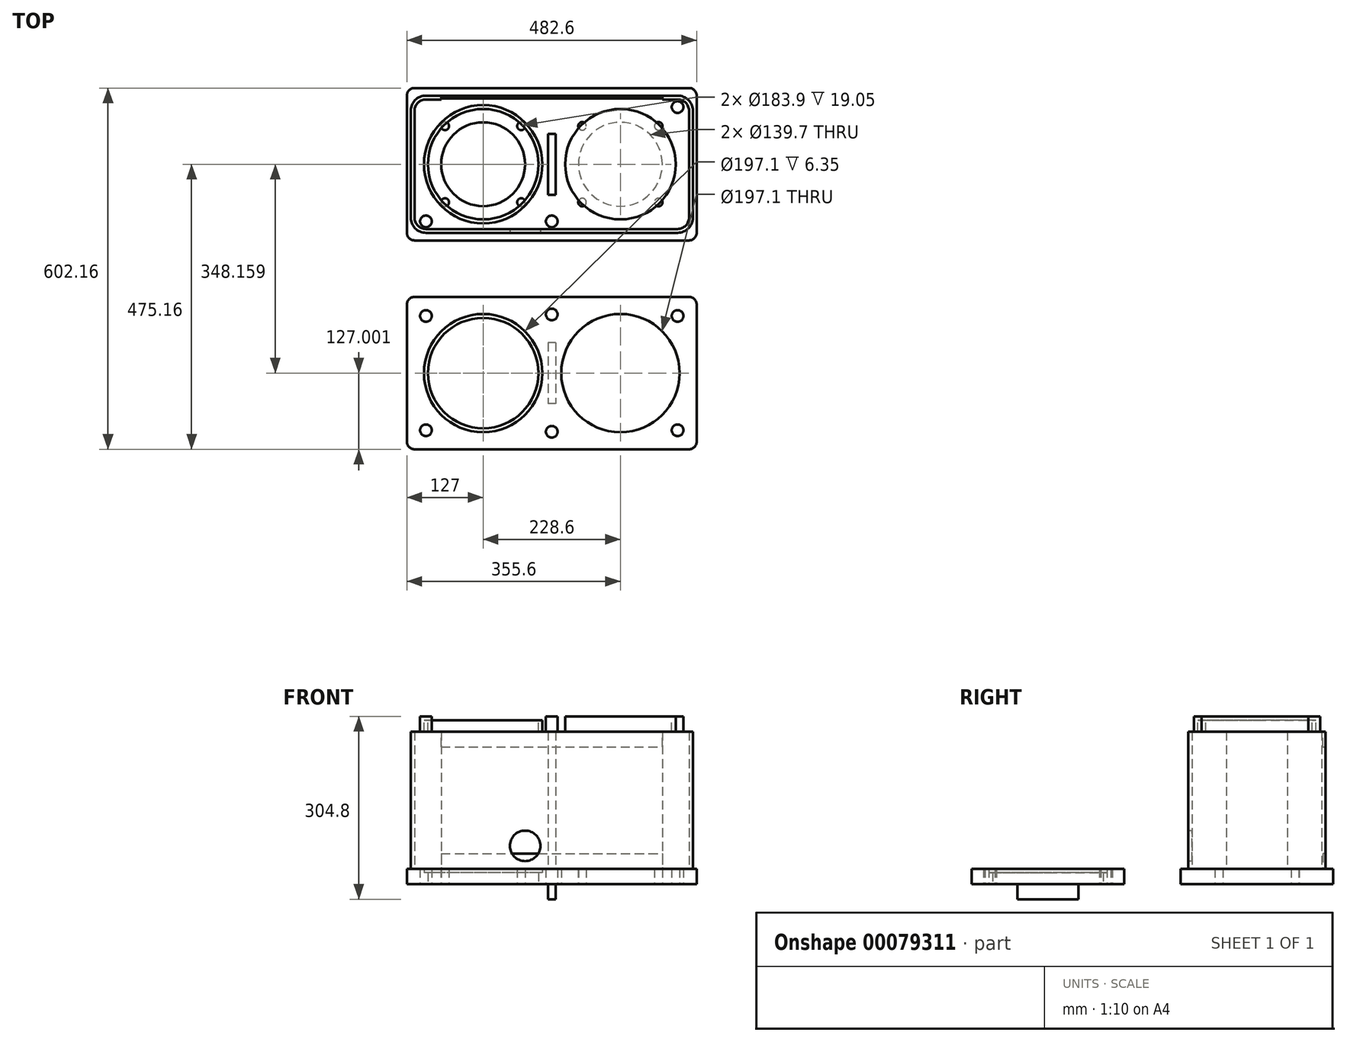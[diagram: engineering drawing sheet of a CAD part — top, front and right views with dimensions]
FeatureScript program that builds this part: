
annotation { "Feature Type Name" : "Feature", "Feature Type Description" : "" }
export const myFeature = defineFeature(function(context is Context, id is Id, definition is map)
    precondition{}
    {
        {
            var Q0;
            Q0=qCreatedBy(makeId("Top.planeOp"),FACE);
            var sketch = newSketch(context, id + "F0", { "sketchPlane" : qUnion([Q0])});
            skLineSegment(sketch, "E0.bottom", {"start": v(241.3, -127) * mm, "end": v(-241.3, -127) * mm});
            skLineSegment(sketch, "E0.top", {"start": v(241.3, 127) * mm, "end": v(-241.3, 127) * mm});
            skLineSegment(sketch, "E0.left", {"start": v(241.3, -127) * mm, "end": v(241.3, 127) * mm});
            skLineSegment(sketch, "E0.right", {"start": v(-241.3, -127) * mm, "end": v(-241.3, 127) * mm});
            skPoint(sketch, "E0.middle", {"position": v(0, 0) * mm});
            skSolve(sketch);
        }
        {
            var Q0;
            Q0=makeQuery(id+"F0.imprint","IMPRINT",FACE,{"disambiguationData":[TD([[makeQuery(id+"F0.imprint","IMPRINT",EDGE,{"derivedFrom":sQuery(id+"F0.wireOp",EDGE,"E0.bottom")}),-1.0]])]});
            extrude(context, id + "F1", {"entities" : qUnion([Q0]), "depth" : 25.4 * mm});
        }
        {
            var Q0;
            Q0=makeQuery(id+"F1.opExtrude","CAP_FACE",FACE,{"disambiguationData":[OSD([sQuery(id+"F0.wireOp",EDGE,"E0.bottom"),sQuery(id+"F0.wireOp",EDGE,"E0.top"),sQuery(id+"F0.wireOp",EDGE,"E0.left"),sQuery(id+"F0.wireOp",EDGE,"E0.right")])],"isStart":false});
            var sketch = newSketch(context, id + "F2", { "sketchPlane" : qUnion([Q0])});
            skLineSegment(sketch, "E1.bottom", {"start": v(209.55, -114.3) * mm, "end": v(-209.55, -114.3) * mm});
            skLineSegment(sketch, "E1.left", {"start": v(234.95, -88.9) * mm, "end": v(234.95, 88.9) * mm});
            skLineSegment(sketch, "E1.right", {"start": v(-234.95, -88.9) * mm, "end": v(-234.95, 88.9) * mm});
            skPoint(sketch, "E1.middle", {"position": v(0, 0) * mm});
            skLineSegment(sketch, "E2.bottom", {"start": v(209.55, -107.95) * mm, "end": v(-209.55, -107.95) * mm});
            skLineSegment(sketch, "E2.left", {"start": v(228.6, -88.9) * mm, "end": v(228.6, 88.9) * mm});
            skLineSegment(sketch, "E2.right", {"start": v(-228.6, -88.9) * mm, "end": v(-228.6, 88.9) * mm});
            skLineSegment(sketch, "E3", {"start": v(-209.55, 114.3) * mm, "end": v(-184.15, 114.3) * mm});
            skLineSegment(sketch, "E4", {"start": v(-209.55, 107.95) * mm, "end": v(-184.14, 107.95) * mm});
            skLineSegment(sketch, "E5", {"start": v(-184.15, 114.3) * mm, "end": v(-184.14, 107.95) * mm});
            skLineSegment(sketch, "E6", {"start": v(209.55, 114.3) * mm, "end": v(184.15, 114.3) * mm});
            skLineSegment(sketch, "E7", {"start": v(184.15, 114.3) * mm, "end": v(184.15, 107.95) * mm});
            skLineSegment(sketch, "E8", {"start": v(184.15, 107.95) * mm, "end": v(209.55, 107.95) * mm});
            skPoint(sketch, "E9.visualSharp", {"position": v(-234.95, 114.3) * mm});
            skArc(sketch, "E9.filletArc", {"start": v(-209.55, 114.3) * mm, "mid": v(-227.51, 106.86) * mm, "end": v(-234.95, 88.9) * mm});
            skPoint(sketch, "E10.visualSharp", {"position": v(-234.95, -114.3) * mm});
            skArc(sketch, "E10.filletArc", {"start": v(-234.95, -88.9) * mm, "mid": v(-227.51, -106.86) * mm, "end": v(-209.55, -114.3) * mm});
            skPoint(sketch, "E11.visualSharp", {"position": v(234.95, -114.3) * mm});
            skArc(sketch, "E11.filletArc", {"start": v(209.55, -114.3) * mm, "mid": v(227.51, -106.86) * mm, "end": v(234.95, -88.9) * mm});
            skPoint(sketch, "E12.visualSharp", {"position": v(234.95, 114.3) * mm});
            skArc(sketch, "E12.filletArc", {"start": v(234.95, 88.9) * mm, "mid": v(227.51, 106.86) * mm, "end": v(209.55, 114.3) * mm});
            skPoint(sketch, "E13.visualSharp", {"position": v(-228.6, 107.95) * mm});
            skArc(sketch, "E13.filletArc", {"start": v(-209.55, 107.95) * mm, "mid": v(-223.02, 102.37) * mm, "end": v(-228.6, 88.9) * mm});
            skPoint(sketch, "E14.visualSharp", {"position": v(-228.6, -107.95) * mm});
            skArc(sketch, "E14.filletArc", {"start": v(-228.6, -88.9) * mm, "mid": v(-223.02, -102.37) * mm, "end": v(-209.55, -107.95) * mm});
            skPoint(sketch, "E15.visualSharp", {"position": v(228.6, -107.95) * mm});
            skArc(sketch, "E15.filletArc", {"start": v(209.55, -107.95) * mm, "mid": v(223.02, -102.37) * mm, "end": v(228.6, -88.9) * mm});
            skPoint(sketch, "E16.visualSharp", {"position": v(228.6, 107.95) * mm});
            skArc(sketch, "E16.filletArc", {"start": v(228.6, 88.9) * mm, "mid": v(223.02, 102.37) * mm, "end": v(209.55, 107.95) * mm});
            skLineSegment(sketch, "E17.bottom", {"start": v(6.35, -50.8) * mm, "end": v(-6.35, -50.8) * mm});
            skLineSegment(sketch, "E17.top", {"start": v(6.35, 50.8) * mm, "end": v(-6.35, 50.8) * mm});
            skLineSegment(sketch, "E17.left", {"start": v(6.35, -50.8) * mm, "end": v(6.35, 50.8) * mm});
            skLineSegment(sketch, "E17.right", {"start": v(-6.35, -50.8) * mm, "end": v(-6.35, 50.8) * mm});
            skSolve(sketch);
        }
        {
            var Q0;
            Q0=makeQuery(id+"F2.imprint","IMPRINT",FACE,{"disambiguationData":[TD([[makeQuery(id+"F2.imprint","IMPRINT",EDGE,{"derivedFrom":sQuery(id+"F2.wireOp",EDGE,"E1.bottom")}),-1.0]])]});
            var Q1;
            Q1=makeQuery(id+"F2.imprint","IMPRINT",FACE,{"disambiguationData":[TD([[makeQuery(id+"F2.imprint","IMPRINT",EDGE,{"derivedFrom":sQuery(id+"F2.wireOp",EDGE,"E17.bottom")}),-1.0]])]});
            extrude(context, id + "F3", {"entities" : qUnion([Q0, Q1]), "operationType" : NewBodyOperationType.ADD, "depth" : 228.6 * mm});
        }
        {
            var Q0;
            Q0=makeQuery(id+"F3.opExtrude","CAP_FACE",FACE,{"disambiguationData":[OSD([sQuery(id+"F2.wireOp",EDGE,"E1.bottom"),sQuery(id+"F2.wireOp",EDGE,"E1.left"),sQuery(id+"F2.wireOp",EDGE,"E1.right"),sQuery(id+"F2.wireOp",EDGE,"E2.bottom"),sQuery(id+"F2.wireOp",EDGE,"E2.left"),sQuery(id+"F2.wireOp",EDGE,"E2.right"),sQuery(id+"F2.wireOp",EDGE,"E3"),sQuery(id+"F2.wireOp",EDGE,"E4"),sQuery(id+"F2.wireOp",EDGE,"E5"),sQuery(id+"F2.wireOp",EDGE,"E6"),sQuery(id+"F2.wireOp",EDGE,"E7"),sQuery(id+"F2.wireOp",EDGE,"E8"),sQuery(id+"F2.wireOp",EDGE,"E9.filletArc"),sQuery(id+"F2.wireOp",EDGE,"E10.filletArc"),sQuery(id+"F2.wireOp",EDGE,"E11.filletArc"),sQuery(id+"F2.wireOp",EDGE,"E12.filletArc"),sQuery(id+"F2.wireOp",EDGE,"E13.filletArc"),sQuery(id+"F2.wireOp",EDGE,"E14.filletArc"),sQuery(id+"F2.wireOp",EDGE,"E15.filletArc"),sQuery(id+"F2.wireOp",EDGE,"E16.filletArc")])],"isStart":false});
            var sketch = newSketch(context, id + "F4", { "sketchPlane" : qUnion([Q0])});
            skLineSegment(sketch, "E18.bottom", {"start": v(241.3, -127) * mm, "end": v(-241.3, -127) * mm});
            skLineSegment(sketch, "E18.top", {"start": v(241.3, 127) * mm, "end": v(-241.3, 127) * mm});
            skLineSegment(sketch, "E18.left", {"start": v(241.3, -127) * mm, "end": v(241.3, 127) * mm});
            skLineSegment(sketch, "E18.right", {"start": v(-241.3, -127) * mm, "end": v(-241.3, 127) * mm});
            skPoint(sketch, "E18.middle", {"position": v(0, 0) * mm});
            skSolve(sketch);
        }
        {
            var Q0;
            Q0=qSketchRegion(id+"F4",true);
            extrude(context, id + "F5", {"entities" : qUnion([Q0]), "operationType" : NewBodyOperationType.ADD, "depth" : 25.4 * mm});
        }
        {
            var Q0;
            Q0=makeQuery(id+"F3.opExtrude","SWEPT_FACE",FACE,{"disambiguationData":[OSD([sQuery(id+"F2.wireOp",EDGE,"E1.bottom")])]});
            var sketch = newSketch(context, id + "F6", { "sketchPlane" : qUnion([Q0])});
            skCircle(sketch, "E19", {"center": v(-44.45, 63.5) * mm, "radius": 25.4 * mm});
            skSolve(sketch);
        }
        {
            var Q0;
            Q0=makeQuery(id+"F6.imprint","IMPRINT",FACE,{"disambiguationData":[TD([[makeQuery(id+"F6.imprint","IMPRINT",EDGE,{"derivedFrom":sQuery(id+"F6.wireOp",EDGE,"E19")}),1.0]])]});
            extrude(context, id + "F7", {"entities" : qUnion([Q0]), "operationType" : NewBodyOperationType.REMOVE, "oppositeDirection" : true, "depth" : 6.35 * mm});
        }
        {
            var Q0;
            Q0=qCreatedBy(makeId("Right.planeOp"),FACE);
            var sketch = newSketch(context, id + "F8", { "sketchPlane" : qUnion([Q0])});
            skLineSegment(sketch, "E20", {"start": v(0, -47.78) * mm, "end": v(0, 307.42) * mm, "construction": true});
            skSolve(sketch);
        }
        {
            var Q0;
            Q0=makeQuery(id+"F5.opExtrude","CAP_FACE",FACE,{"disambiguationData":[OSD([sQuery(id+"F4.wireOp",EDGE,"E18.bottom"),sQuery(id+"F4.wireOp",EDGE,"E18.top"),sQuery(id+"F4.wireOp",EDGE,"E18.left"),sQuery(id+"F4.wireOp",EDGE,"E18.right")])],"isStart":false});
            var sketch = newSketch(context, id + "F9", { "sketchPlane" : qUnion([Q0])});
            skLineSegment(sketch, "E21", {"start": v(0, 148.36) * mm, "end": v(0, -160.24) * mm, "construction": true});
            skPoint(sketch, "E21.endSnap0", {"position": v(0, -127) * mm});
            skLineSegment(sketch, "E22", {"start": v(-277.11, 0) * mm, "end": v(283.69, 0) * mm, "construction": true});
            skPoint(sketch, "E22.startSnap0", {"position": v(-241.3, 0) * mm});
            skPoint(sketch, "E22.endSnap0", {"position": v(-241.3, 0) * mm});
            skCircle(sketch, "E23", {"center": v(-114.3, 0) * mm, "radius": 98.55 * mm});
            skCircle(sketch, "E24", {"center": v(-114.3, 0) * mm, "radius": 91.95 * mm});
            skCircle(sketch, "E25", {"center": v(-209.55, 95.25) * mm, "radius": 9.72 * mm});
            skCircle(sketch, "E26", {"center": v(0, 95.25) * mm, "radius": 9.72 * mm});
            skCircle(sketch, "E27.MirrorC", {"center": v(114.3, 0) * mm, "radius": 98.55 * mm});
            skCircle(sketch, "E28.MirrorC", {"center": v(114.3, 0) * mm, "radius": 91.95 * mm});
            skCircle(sketch, "E29.MirrorC", {"center": v(209.55, 95.25) * mm, "radius": 9.72 * mm});
            skCircle(sketch, "E30.MirrorC", {"center": v(-209.55, -95.25) * mm, "radius": 9.72 * mm});
            skCircle(sketch, "E31.MirrorC", {"center": v(0, -95.25) * mm, "radius": 9.72 * mm});
            skCircle(sketch, "E32.MirrorC", {"center": v(209.55, -95.25) * mm, "radius": 9.72 * mm});
            skSolve(sketch);
        }
        {
            var Q0;
            Q0=makeQuery(id+"F9.imprint","IMPRINT",FACE,{"disambiguationData":[TD([[makeQuery(id+"F9.imprint","IMPRINT",EDGE,{"derivedFrom":sQuery(id+"F9.wireOp",EDGE,"E25")}),1.0]])]});
            var Q1;
            Q1=makeQuery(id+"F9.imprint","IMPRINT",FACE,{"disambiguationData":[TD([[makeQuery(id+"F9.imprint","IMPRINT",EDGE,{"derivedFrom":sQuery(id+"F9.wireOp",EDGE,"E26")}),1.0]])]});
            var Q2;
            Q2=makeQuery(id+"F9.imprint","IMPRINT",FACE,{"disambiguationData":[TD([[makeQuery(id+"F9.imprint","IMPRINT",EDGE,{"derivedFrom":sQuery(id+"F9.wireOp",EDGE,"E24")}),1.0]])]});
            var Q3;
            Q3=makeQuery(id+"F9.imprint","IMPRINT",FACE,{"disambiguationData":[TD([[makeQuery(id+"F9.imprint","IMPRINT",EDGE,{"derivedFrom":sQuery(id+"F9.wireOp",EDGE,"E28.MirrorC")}),-1.0]])]});
            var Q4;
            Q4=makeQuery(id+"F9.imprint","IMPRINT",FACE,{"disambiguationData":[TD([[makeQuery(id+"F9.imprint","IMPRINT",EDGE,{"derivedFrom":sQuery(id+"F9.wireOp",EDGE,"E29.MirrorC")}),-1.0]])]});
            var Q5;
            Q5=makeQuery(id+"F9.imprint","IMPRINT",FACE,{"disambiguationData":[TD([[makeQuery(id+"F9.imprint","IMPRINT",EDGE,{"derivedFrom":sQuery(id+"F9.wireOp",EDGE,"E32.MirrorC")}),1.0]])]});
            var Q6;
            Q6=makeQuery(id+"F9.imprint","IMPRINT",FACE,{"disambiguationData":[TD([[makeQuery(id+"F9.imprint","IMPRINT",EDGE,{"derivedFrom":sQuery(id+"F9.wireOp",EDGE,"E31.MirrorC")}),-1.0]])]});
            var Q7;
            Q7=makeQuery(id+"F9.imprint","IMPRINT",FACE,{"disambiguationData":[TD([[makeQuery(id+"F9.imprint","IMPRINT",EDGE,{"derivedFrom":sQuery(id+"F9.wireOp",EDGE,"E30.MirrorC")}),-1.0]])]});
            extrude(context, id + "F10", {"entities" : qUnion([Q0, Q1, Q2, Q3, Q4, Q5, Q6, Q7]), "operationType" : NewBodyOperationType.REMOVE, "oppositeDirection" : true, "depth" : 25.4 * mm});
        }
        {
            var Q0;
            Q0=makeQuery(id+"F9.imprint","IMPRINT",FACE,{"disambiguationData":[TD([[makeQuery(id+"F9.imprint","IMPRINT",EDGE,{"derivedFrom":sQuery(id+"F9.wireOp",EDGE,"E23")}),1.0]])]});
            var Q1;
            Q1=makeQuery(id+"F9.imprint","IMPRINT",FACE,{"disambiguationData":[TD([[makeQuery(id+"F9.imprint","IMPRINT",EDGE,{"derivedFrom":sQuery(id+"F9.wireOp",EDGE,"E27.MirrorC")}),-1.0]])]});
            extrude(context, id + "F11", {"entities" : qUnion([Q0, Q1]), "operationType" : NewBodyOperationType.REMOVE, "oppositeDirection" : true, "depth" : 6.35 * mm});
        }
        {
            var Q0;
            Q0=makeQuery(id+"F1.opExtrude","CAP_FACE",FACE,{"disambiguationData":[OSD([sQuery(id+"F0.wireOp",EDGE,"E0.bottom"),sQuery(id+"F0.wireOp",EDGE,"E0.top"),sQuery(id+"F0.wireOp",EDGE,"E0.left"),sQuery(id+"F0.wireOp",EDGE,"E0.right")])],"isStart":true});
            var sketch = newSketch(context, id + "F12", { "sketchPlane" : qUnion([Q0])});
            skLineSegment(sketch, "E33", {"start": v(270.27, 0) * mm, "end": v(-270.6, 0) * mm, "construction": true});
            skPoint(sketch, "E33.endSnap0", {"position": v(241.3, 0) * mm});
            skLineSegment(sketch, "E34", {"start": v(0, -143.09) * mm, "end": v(0, 149.51) * mm, "construction": true});
            skPoint(sketch, "E34.endSnap0", {"position": v(0, 127) * mm});
            skCircle(sketch, "E35", {"center": v(114.3, 0) * mm, "radius": 69.85 * mm});
            skLineSegment(sketch, "E36", {"start": v(114.3, 0) * mm, "end": v(177.8, -63.5) * mm, "construction": true});
            skCircle(sketch, "E37", {"center": v(177.8, -63.5) * mm, "radius": 6.75 * mm});
            skCircle(sketch, "E38.1.0", {"center": v(177.8, 63.5) * mm, "radius": 6.75 * mm});
            skCircle(sketch, "E38.2.0", {"center": v(50.8, 63.5) * mm, "radius": 6.75 * mm});
            skCircle(sketch, "E38.3.0", {"center": v(50.8, -63.5) * mm, "radius": 6.75 * mm});
            skCircle(sketch, "E39.MirrorC", {"center": v(-50.8, -63.5) * mm, "radius": 6.75 * mm});
            skCircle(sketch, "E40.MirrorC", {"center": v(-114.3, 0) * mm, "radius": 69.85 * mm});
            skCircle(sketch, "E41.MirrorC", {"center": v(-50.8, 63.5) * mm, "radius": 6.75 * mm});
            skCircle(sketch, "E42.MirrorC", {"center": v(-177.8, 63.5) * mm, "radius": 6.75 * mm});
            skCircle(sketch, "E43.MirrorC", {"center": v(-177.8, -63.5) * mm, "radius": 6.75 * mm});
            skSolve(sketch);
        }
        {
            var Q0;
            Q0 = qSketchRegion(id + "F12", true);
            extrude(context, id + "F13", {"entities" : qUnion([Q0]), "operationType" : NewBodyOperationType.REMOVE, "oppositeDirection" : true, "depth" : 25.4 * mm});
        }
        {
            var Q0;
            Q0=makeQuery(id+"F1.opExtrude","CAP_FACE",FACE,{"disambiguationData":[OSD([sQuery(id+"F0.wireOp",EDGE,"E0.bottom"),sQuery(id+"F0.wireOp",EDGE,"E0.top"),sQuery(id+"F0.wireOp",EDGE,"E0.left"),sQuery(id+"F0.wireOp",EDGE,"E0.right")])],"isStart":false});
            var sketch = newSketch(context, id + "F14", { "sketchPlane" : qUnion([Q0])});
            skLineSegment(sketch, "E44.bottom", {"start": v(-184.15, 114.3) * mm, "end": v(184.15, 114.3) * mm});
            skLineSegment(sketch, "E44.top", {"start": v(-184.15, 109.54) * mm, "end": v(184.15, 109.54) * mm});
            skLineSegment(sketch, "E44.left", {"start": v(-184.15, 114.3) * mm, "end": v(-184.15, 109.54) * mm});
            skLineSegment(sketch, "E44.right", {"start": v(184.15, 114.3) * mm, "end": v(184.15, 109.54) * mm});
            skSolve(sketch);
        }
        {
            var Q0;
            {var subQ0=sQuery(id+"F14.wireOp",EDGE,"E44.bottom");Q0=makeQuery(id+"F14.imprint","IMPRINT",FACE,{"disambiguationData":[TD([[makeQuery(id+"F14.imprint","IMPRINT",EDGE,{"derivedFrom":subQ0}),-1.0]])]});}
            extrude(context, id + "F15", {"entities" : qUnion([Q0]), "depth" : 25.4 * mm});
        }
        {
            var Q0;
            Q0=makeQuery(id+"F5.opExtrude","CAP_FACE",FACE,{"disambiguationData":[OSD([sQuery(id+"F4.wireOp",EDGE,"E18.bottom"),sQuery(id+"F4.wireOp",EDGE,"E18.top"),sQuery(id+"F4.wireOp",EDGE,"E18.left"),sQuery(id+"F4.wireOp",EDGE,"E18.right")])],"isStart":true});
            var sketch = newSketch(context, id + "F16", { "sketchPlane" : qUnion([Q0])});
            skLineSegment(sketch, "E45.bottom", {"start": v(-184.15, -109.54) * mm, "end": v(184.15, -109.54) * mm});
            skLineSegment(sketch, "E45.top", {"start": v(-184.15, -114.3) * mm, "end": v(184.15, -114.3) * mm});
            skLineSegment(sketch, "E45.left", {"start": v(-184.15, -109.54) * mm, "end": v(-184.15, -114.3) * mm});
            skLineSegment(sketch, "E45.right", {"start": v(184.15, -109.54) * mm, "end": v(184.15, -114.3) * mm});
            skPoint(sketch, "E45.middle", {"position": v(0, -111.92) * mm});
            skSolve(sketch);
        }
        {
            var Q0;
            {var subQ4=sQuery(id+"F16.wireOp",EDGE,"E45.top");Q0=makeQuery(id+"F16.imprint","IMPRINT",FACE,{"disambiguationData":[TD([[makeQuery(id+"F16.imprint","IMPRINT",EDGE,{"derivedFrom":subQ4}),1.0]])]});}
            extrude(context, id + "F17", {"entities" : qUnion([Q0]), "depth" : 25.4 * mm});
        }
        {
            var Q0;
            Q0=qCreatedBy(makeId("Top.planeOp"),FACE);
            var sketch = newSketch(context, id + "F18", { "sketchPlane" : qUnion([Q0])});
            skLineSegment(sketch, "E46.bottom", {"start": v(241.3, -475.16) * mm, "end": v(-241.3, -475.16) * mm});
            skLineSegment(sketch, "E46.top", {"start": v(241.3, -221.16) * mm, "end": v(-241.3, -221.16) * mm});
            skLineSegment(sketch, "E46.left", {"start": v(241.3, -475.16) * mm, "end": v(241.3, -221.16) * mm});
            skLineSegment(sketch, "E46.right", {"start": v(-241.3, -475.16) * mm, "end": v(-241.3, -221.16) * mm});
            skPoint(sketch, "E46.middle", {"position": v(0, -348.16) * mm});
            skLineSegment(sketch, "E47", {"start": v(0, -197.28) * mm, "end": v(0, -505.88) * mm, "construction": true});
            skPoint(sketch, "E47.endSnap0", {"position": v(0, -472.64) * mm});
            skLineSegment(sketch, "E48", {"start": v(-277.11, -348.16) * mm, "end": v(283.69, -348.16) * mm, "construction": true});
            skPoint(sketch, "E48.startSnap0", {"position": v(-247.65, -348.16) * mm});
            skPoint(sketch, "E48.endSnap0", {"position": v(-247.65, -348.16) * mm});
            skCircle(sketch, "E49", {"center": v(-114.3, -348.16) * mm, "radius": 98.55 * mm});
            skCircle(sketch, "E50", {"center": v(-114.3, -348.16) * mm, "radius": 91.95 * mm});
            skCircle(sketch, "E51", {"center": v(-209.55, -252.9) * mm, "radius": 9.72 * mm});
            skCircle(sketch, "E52", {"center": v(0, -250.39) * mm, "radius": 9.72 * mm});
            skCircle(sketch, "E53.MirrorC", {"center": v(114.3, -348.16) * mm, "radius": 98.55 * mm});
            skCircle(sketch, "E54.MirrorC", {"center": v(114.3, -348.16) * mm, "radius": 91.95 * mm});
            skCircle(sketch, "E55.MirrorC", {"center": v(209.55, -252.9) * mm, "radius": 9.72 * mm});
            skCircle(sketch, "E56.MirrorC", {"center": v(-209.55, -443.4) * mm, "radius": 9.72 * mm});
            skCircle(sketch, "E57.MirrorC", {"center": v(0, -445.93) * mm, "radius": 9.72 * mm});
            skCircle(sketch, "E58.MirrorC", {"center": v(209.55, -443.4) * mm, "radius": 9.72 * mm});
            skSolve(sketch);
        }
        {
            var Q0;
            Q0=makeQuery(id+"F18.imprint","IMPRINT",FACE,{"disambiguationData":[TD([[makeQuery(id+"F18.imprint","IMPRINT",EDGE,{"derivedFrom":sQuery(id+"F18.wireOp",EDGE,"E46.bottom")}),-1.0]])]});
            extrude(context, id + "F19", {"entities" : qUnion([Q0]), "depth" : 25.4 * mm});
        }
        {
            var Q0;
            Q0=makeQuery(id+"F18.imprint","IMPRINT",FACE,{"disambiguationData":[TD([[makeQuery(id+"F18.imprint","IMPRINT",EDGE,{"derivedFrom":sQuery(id+"F18.wireOp",EDGE,"E53.MirrorC")}),-1.0]])]});
            var Q1;
            Q1=makeQuery(id+"F18.imprint","IMPRINT",FACE,{"disambiguationData":[TD([[makeQuery(id+"F18.imprint","IMPRINT",EDGE,{"derivedFrom":sQuery(id+"F18.wireOp",EDGE,"E49")}),1.0]])]});
            extrude(context, id + "F20", {"entities" : qUnion([Q0, Q1]), "operationType" : NewBodyOperationType.ADD, "depth" : 19.05 * mm});
        }
        {
            var Q0;
            {var subQ0=sQuery(id+"F18.wireOp",EDGE,"E53.MirrorC");var subQ1=sQuery(id+"F18.wireOp",EDGE,"E49");Q0=makeQuery(id+"F20.boolean.opBoolean","MERGE",FACE,{"derivedFrom":[makeQuery(id+"F19.opExtrude","CAP_FACE",FACE,{"disambiguationData":[OSD([sQuery(id+"F18.wireOp",EDGE,"E46.bottom"),sQuery(id+"F18.wireOp",EDGE,"E46.top"),sQuery(id+"F18.wireOp",EDGE,"E46.left"),sQuery(id+"F18.wireOp",EDGE,"E46.right"),subQ1,sQuery(id+"F18.wireOp",EDGE,"E51"),sQuery(id+"F18.wireOp",EDGE,"E52"),subQ0,sQuery(id+"F18.wireOp",EDGE,"E55.MirrorC"),sQuery(id+"F18.wireOp",EDGE,"E56.MirrorC"),sQuery(id+"F18.wireOp",EDGE,"E57.MirrorC"),sQuery(id+"F18.wireOp",EDGE,"E58.MirrorC")])],"isStart":true}),makeQuery(id+"F20.opExtrude","CAP_FACE",FACE,{"disambiguationData":[OSD([subQ1,sQuery(id+"F18.wireOp",EDGE,"E50")])],"isStart":true}),makeQuery(id+"F20.opExtrude","CAP_FACE",FACE,{"disambiguationData":[OSD([subQ0,sQuery(id+"F18.wireOp",EDGE,"E54.MirrorC")])],"isStart":true})]});}
            var sketch = newSketch(context, id + "F21", { "sketchPlane" : qUnion([Q0])});
            skLineSegment(sketch, "E59.bottom", {"start": v(6.35, 297.36) * mm, "end": v(-6.35, 297.36) * mm});
            skLineSegment(sketch, "E59.top", {"start": v(6.35, 398.96) * mm, "end": v(-6.35, 398.96) * mm});
            skLineSegment(sketch, "E59.left", {"start": v(6.35, 297.36) * mm, "end": v(6.35, 398.96) * mm});
            skLineSegment(sketch, "E59.right", {"start": v(-6.35, 297.36) * mm, "end": v(-6.35, 398.96) * mm});
            skPoint(sketch, "E59.middle", {"position": v(0, 348.16) * mm});
            skSolve(sketch);
        }
        {
            var Q0;
            Q0 = qSketchRegion(id + "F21", true);
            extrude(context, id + "F22", {"entities" : qUnion([Q0]), "operationType" : NewBodyOperationType.ADD, "depth" : 25.4 * mm});
        }
        {
            var Q0;
            Q0=makeQuery(id+"F5.opExtrude","SWEPT_EDGE",EDGE,{"disambiguationData":[OSD([sQuery(id+"F4.wireOp",EDGE,"E18.top"),sQuery(id+"F4.wireOp",EDGE,"E18.left")])]});
            var Q1;
            Q1=makeQuery(id+"F5.opExtrude","SWEPT_EDGE",EDGE,{"disambiguationData":[OSD([sQuery(id+"F4.wireOp",EDGE,"E18.bottom"),sQuery(id+"F4.wireOp",EDGE,"E18.left")])]});
            var Q2;
            Q2=makeQuery(id+"F1.opExtrude","SWEPT_EDGE",EDGE,{"disambiguationData":[OSD([sQuery(id+"F0.wireOp",EDGE,"E0.top"),sQuery(id+"F0.wireOp",EDGE,"E0.left")])]});
            var Q3;
            Q3=makeQuery(id+"F1.opExtrude","SWEPT_EDGE",EDGE,{"disambiguationData":[OSD([sQuery(id+"F0.wireOp",EDGE,"E0.bottom"),sQuery(id+"F0.wireOp",EDGE,"E0.left")])]});
            var Q4;
            Q4=makeQuery(id+"F5.opExtrude","SWEPT_EDGE",EDGE,{"disambiguationData":[OSD([sQuery(id+"F4.wireOp",EDGE,"E18.bottom"),sQuery(id+"F4.wireOp",EDGE,"E18.right")])]});
            var Q5;
            Q5=makeQuery(id+"F5.opExtrude","SWEPT_EDGE",EDGE,{"disambiguationData":[OSD([sQuery(id+"F4.wireOp",EDGE,"E18.top"),sQuery(id+"F4.wireOp",EDGE,"E18.right")])]});
            var Q6;
            Q6=makeQuery(id+"F1.opExtrude","SWEPT_EDGE",EDGE,{"disambiguationData":[OSD([sQuery(id+"F0.wireOp",EDGE,"E0.top"),sQuery(id+"F0.wireOp",EDGE,"E0.right")])]});
            var Q7;
            Q7=makeQuery(id+"F1.opExtrude","SWEPT_EDGE",EDGE,{"disambiguationData":[OSD([sQuery(id+"F0.wireOp",EDGE,"E0.bottom"),sQuery(id+"F0.wireOp",EDGE,"E0.right")])]});
            var Q8;
            Q8=makeQuery(id+"F19.opExtrude","SWEPT_EDGE",EDGE,{"disambiguationData":[OSD([sQuery(id+"F18.wireOp",EDGE,"E46.top"),sQuery(id+"F18.wireOp",EDGE,"E46.right")])]});
            var Q9;
            Q9=makeQuery(id+"F19.opExtrude","SWEPT_EDGE",EDGE,{"disambiguationData":[OSD([sQuery(id+"F18.wireOp",EDGE,"E46.bottom"),sQuery(id+"F18.wireOp",EDGE,"E46.right")])]});
            var Q10;
            Q10=makeQuery(id+"F19.opExtrude","SWEPT_EDGE",EDGE,{"disambiguationData":[OSD([sQuery(id+"F18.wireOp",EDGE,"E46.top"),sQuery(id+"F18.wireOp",EDGE,"E46.left")])]});
            var Q11;
            Q11=makeQuery(id+"F19.opExtrude","SWEPT_EDGE",EDGE,{"disambiguationData":[OSD([sQuery(id+"F18.wireOp",EDGE,"E46.bottom"),sQuery(id+"F18.wireOp",EDGE,"E46.left")])]});
            fillet(context, id + "F23", {"entities" : qUnion([Q0, Q1, Q2, Q3, Q4, Q5, Q6, Q7, Q8, Q9, Q10, Q11]), "radius" : 12.7 * mm, "tangentPropagation" : true, "allowEdgeOverflow" : false});
        }
    });
